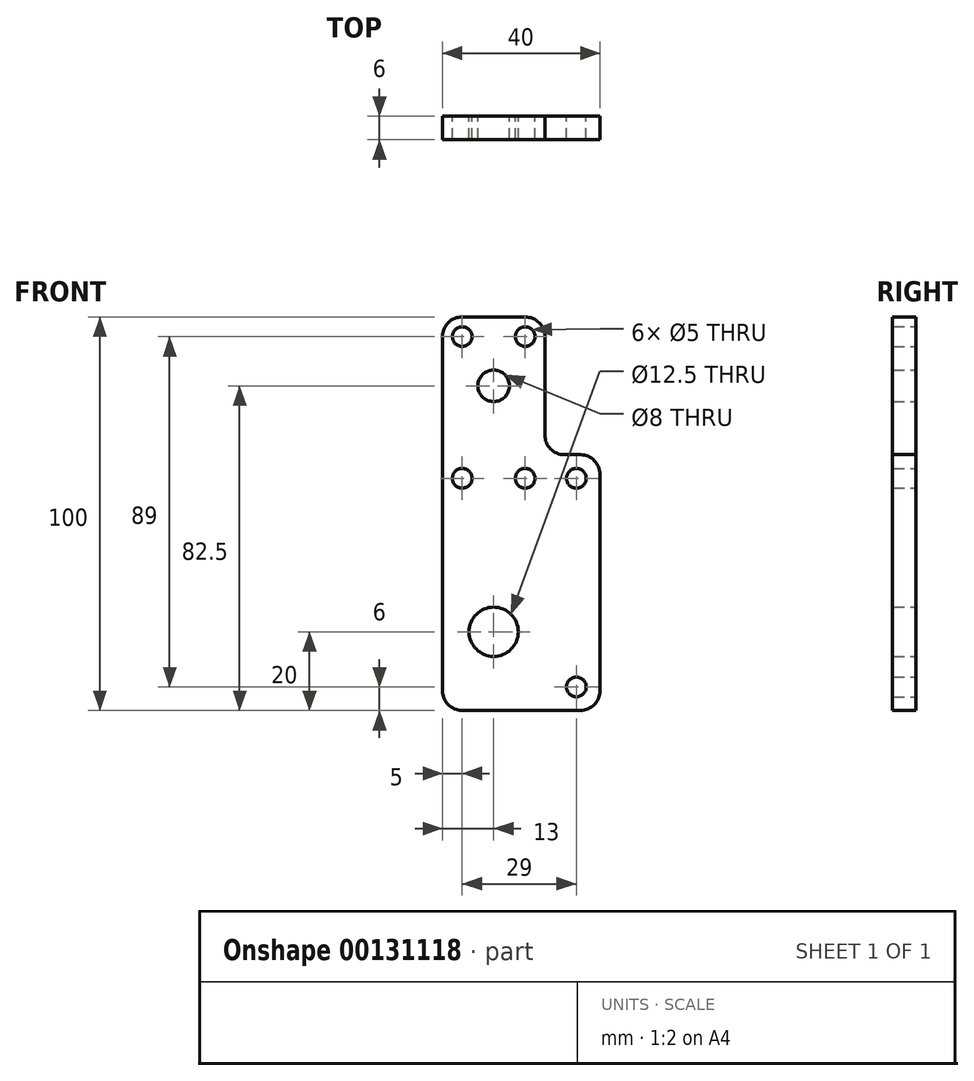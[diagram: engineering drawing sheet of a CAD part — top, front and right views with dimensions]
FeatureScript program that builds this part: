
annotation { "Feature Type Name" : "Feature", "Feature Type Description" : "" }
export const myFeature = defineFeature(function(context is Context, id is Id, definition is map)
    precondition{}
    {
        {
            var Q0;
            Q0=qCreatedBy(makeId("Front.planeOp"),FACE);
            var sketch = newSketch(context, id + "F0", { "sketchPlane" : qUnion([Q0])});
            skLineSegment(sketch, "E0.bottom", {"start": v(0, 27) * mm, "end": v(13, 27) * mm, "construction": true});
            skLineSegment(sketch, "E0.top", {"start": v(0, -27) * mm, "end": v(13, -27) * mm});
            skLineSegment(sketch, "E0.right", {"start": v(13, 27) * mm, "end": v(13, -27) * mm, "construction": true});
            skLineSegment(sketch, "E1", {"start": v(26, 38) * mm, "end": v(40, 38) * mm});
            skLineSegment(sketch, "E2", {"start": v(40, 38) * mm, "end": v(40, -27) * mm});
            skLineSegment(sketch, "E3", {"start": v(40, -27) * mm, "end": v(13, -27) * mm});
            skLineSegment(sketch, "E4", {"start": v(0, 27) * mm, "end": v(0, -27) * mm});
            skPoint(sketch, "E5", {"position": v(13, -7) * mm});
            skLineSegment(sketch, "E6", {"start": v(34, -27) * mm, "end": v(34, 38) * mm, "construction": true});
            skPoint(sketch, "E7", {"position": v(34, -21) * mm});
            skPoint(sketch, "E8", {"position": v(34, 32) * mm});
            skLineSegment(sketch, "E9", {"start": v(5, -27) * mm, "end": v(5, 32) * mm, "construction": true});
            skPoint(sketch, "E10", {"position": v(5, 32) * mm});
            skLineSegment(sketch, "E11", {"start": v(5, 32) * mm, "end": v(21, 32) * mm, "construction": true});
            skPoint(sketch, "E12", {"position": v(21, 32) * mm});
            skPoint(sketch, "E13", {"position": v(26, 38) * mm});
            skLineSegment(sketch, "E14", {"start": v(26, 38) * mm, "end": v(26, 73) * mm});
            skLineSegment(sketch, "E15", {"start": v(26, 73) * mm, "end": v(0, 73) * mm});
            skPoint(sketch, "E16.end.orphan", {"position": v(0, 38) * mm});
            skLineSegment(sketch, "E17", {"start": v(0, 27) * mm, "end": v(0, 73) * mm});
            skPoint(sketch, "E18", {"position": v(5, 68) * mm});
            skPoint(sketch, "E19", {"position": v(21, 68) * mm});
            skPoint(sketch, "E20", {"position": v(13, 55.5) * mm});
            skSolve(sketch);
        }
        {
            var Q0;
            Q0=makeQuery(id+"F0.imprint","IMPRINT",FACE,{"disambiguationData":[TD([[makeQuery(id+"F0.imprint","IMPRINT",EDGE,{"derivedFrom":sQuery(id+"F0.wireOp",EDGE,"E0.top")}),1.0]])]});
            extrude(context, id + "F1", {"entities" : qUnion([Q0]), "depth" : 6 * mm});
        }
        {
            var Q0;
            Q0=sQuery(id+"F0.wireOp",VERTEX,"E5");
            var Q1;
            Q1=makeQuery(id+"F1.opExtrude","SWEPT_BODY",BODY,{"disambiguationData":[OSD([sQuery(id+"F0.wireOp",EDGE,"E0.top"),sQuery(id+"F0.wireOp",EDGE,"E1"),sQuery(id+"F0.wireOp",EDGE,"E2"),sQuery(id+"F0.wireOp",EDGE,"E3"),sQuery(id+"F0.wireOp",EDGE,"E4")])]});
            hole(context, id + "F2", {"style" : HoleStyle.SIMPLE, "endStyle" : HoleEndStyle.THROUGH, "oppositeDirection" : true, "holeDiameter" : 12.5 * mm, "locations" : qUnion([Q0]), "scope" : qUnion([Q1]), "isTappedThrough" : true});
        }
        {
            var Q0;
            Q0=sQuery(id+"F0.wireOp",VERTEX,"E7");
            var Q1;
            Q1=sQuery(id+"F0.wireOp",VERTEX,"E8");
            var Q2;
            Q2=makeQuery(id+"F1.opExtrude","SWEPT_BODY",BODY,{"disambiguationData":[OSD([sQuery(id+"F0.wireOp",EDGE,"E0.top"),sQuery(id+"F0.wireOp",EDGE,"E1"),sQuery(id+"F0.wireOp",EDGE,"E2"),sQuery(id+"F0.wireOp",EDGE,"E3"),sQuery(id+"F0.wireOp",EDGE,"E4")])]});
            hole(context, id + "F3", {"style" : HoleStyle.SIMPLE, "endStyle" : HoleEndStyle.THROUGH, "oppositeDirection" : true, "holeDiameter" : 5 * mm, "locations" : qUnion([Q0, Q1]), "scope" : qUnion([Q2]), "isTappedThrough" : true});
        }
        {
            var Q0;
            Q0=sQuery(id+"F0.wireOp",VERTEX,"E10");
            var Q1;
            Q1=sQuery(id+"F0.wireOp",VERTEX,"E12");
            var Q2;
            Q2=makeQuery(id+"F1.opExtrude","SWEPT_BODY",BODY,{"disambiguationData":[OSD([sQuery(id+"F0.wireOp",EDGE,"E0.top"),sQuery(id+"F0.wireOp",EDGE,"E1"),sQuery(id+"F0.wireOp",EDGE,"E2"),sQuery(id+"F0.wireOp",EDGE,"E3"),sQuery(id+"F0.wireOp",EDGE,"E4")])]});
            hole(context, id + "F4", {"style" : HoleStyle.SIMPLE, "endStyle" : HoleEndStyle.THROUGH, "oppositeDirection" : true, "holeDiameter" : 5 * mm, "locations" : qUnion([Q0, Q1]), "scope" : qUnion([Q2]), "isTappedThrough" : true});
        }
        {
            var Q0;
            Q0=sQuery(id+"F0.wireOp",VERTEX,"E18");
            var Q1;
            Q1=sQuery(id+"F0.wireOp",VERTEX,"E19");
            var Q2;
            Q2=makeQuery(id+"F1.opExtrude","SWEPT_BODY",BODY,{"disambiguationData":[OSD([sQuery(id+"F0.wireOp",EDGE,"E0.top"),sQuery(id+"F0.wireOp",EDGE,"E1"),sQuery(id+"F0.wireOp",EDGE,"E2"),sQuery(id+"F0.wireOp",EDGE,"E3"),sQuery(id+"F0.wireOp",EDGE,"E4"),sQuery(id+"F0.wireOp",EDGE,"E14"),sQuery(id+"F0.wireOp",EDGE,"E15"),sQuery(id+"F0.wireOp",EDGE,"E17")])]});
            hole(context, id + "F5", {"style" : HoleStyle.SIMPLE, "endStyle" : HoleEndStyle.THROUGH, "oppositeDirection" : true, "holeDiameter" : 5 * mm, "locations" : qUnion([Q0, Q1]), "scope" : qUnion([Q2]), "isTappedThrough" : true});
        }
        {
            var Q0;
            Q0=makeQuery(id+"F1.opExtrude","SWEPT_EDGE",EDGE,{"disambiguationData":[OSD([sQuery(id+"F0.wireOp",EDGE,"E15"),sQuery(id+"F0.wireOp",EDGE,"E17")])]});
            var Q1;
            Q1=makeQuery(id+"F1.opExtrude","SWEPT_EDGE",EDGE,{"disambiguationData":[OSD([sQuery(id+"F0.wireOp",EDGE,"E14"),sQuery(id+"F0.wireOp",EDGE,"E15")])]});
            var Q2;
            Q2=makeQuery(id+"F1.opExtrude","SWEPT_EDGE",EDGE,{"disambiguationData":[OSD([sQuery(id+"F0.wireOp",EDGE,"E1"),sQuery(id+"F0.wireOp",EDGE,"E14")])]});
            var Q3;
            Q3=makeQuery(id+"F1.opExtrude","SWEPT_EDGE",EDGE,{"disambiguationData":[OSD([sQuery(id+"F0.wireOp",EDGE,"E1"),sQuery(id+"F0.wireOp",EDGE,"E2")])]});
            var Q4;
            Q4=makeQuery(id+"F1.opExtrude","SWEPT_EDGE",EDGE,{"disambiguationData":[OSD([sQuery(id+"F0.wireOp",EDGE,"E2"),sQuery(id+"F0.wireOp",EDGE,"E3")])]});
            var Q5;
            Q5=makeQuery(id+"F1.opExtrude","SWEPT_EDGE",EDGE,{"disambiguationData":[OSD([sQuery(id+"F0.wireOp",EDGE,"E0.top"),sQuery(id+"F0.wireOp",EDGE,"E4")])]});
            fillet(context, id + "F6", {"entities" : qUnion([Q0, Q1, Q2, Q3, Q4, Q5]), "radius" : 5 * mm, "tangentPropagation" : true, "allowEdgeOverflow" : false});
        }
        {
            var Q0;
            Q0=sQuery(id+"F0.wireOp",VERTEX,"E20");
            var Q1;
            Q1=makeQuery(id+"F1.opExtrude","SWEPT_BODY",BODY,{"disambiguationData":[OSD([sQuery(id+"F0.wireOp",EDGE,"E0.top"),sQuery(id+"F0.wireOp",EDGE,"E1"),sQuery(id+"F0.wireOp",EDGE,"E2"),sQuery(id+"F0.wireOp",EDGE,"E3"),sQuery(id+"F0.wireOp",EDGE,"E4"),sQuery(id+"F0.wireOp",EDGE,"E14"),sQuery(id+"F0.wireOp",EDGE,"E15"),sQuery(id+"F0.wireOp",EDGE,"E17")])]});
            hole(context, id + "F7", {"style" : HoleStyle.SIMPLE, "endStyle" : HoleEndStyle.BLIND, "oppositeDirection" : true, "holeDiameter" : 8 * mm, "holeDepth" : 20 * mm, "locations" : qUnion([Q0]), "scope" : qUnion([Q1])});
        }
    });
